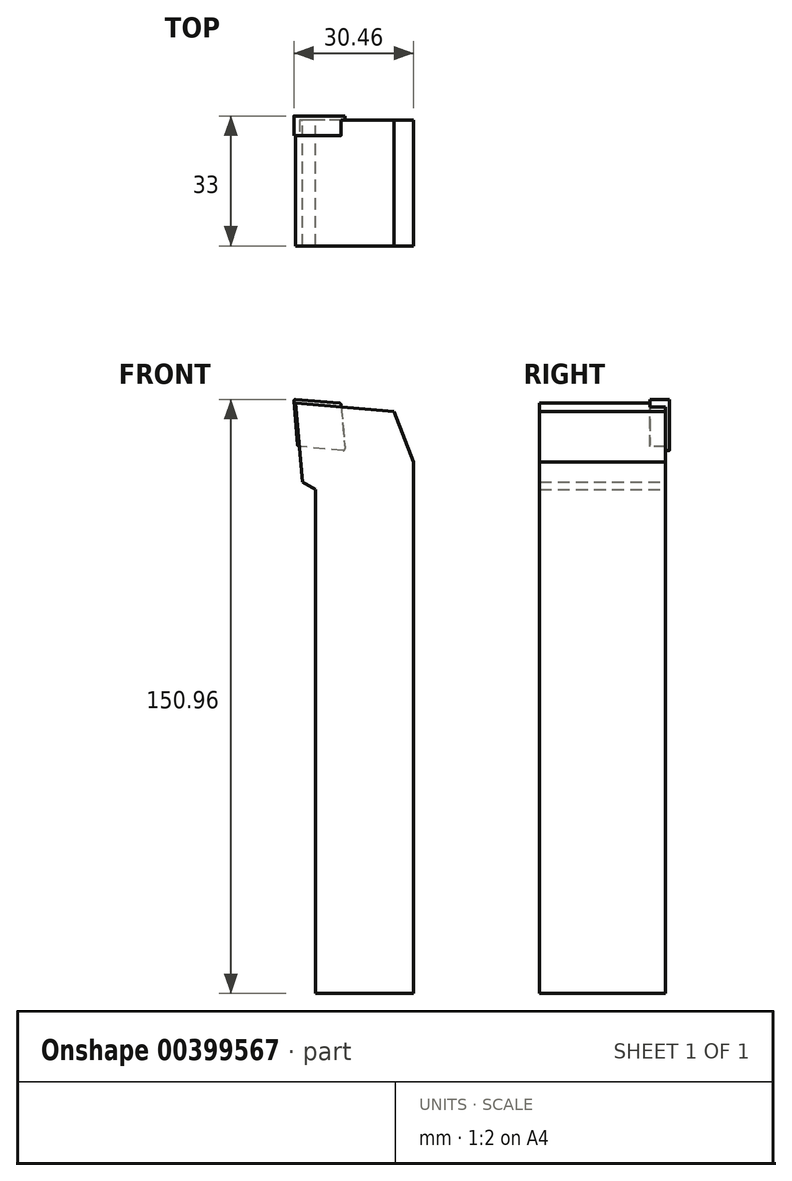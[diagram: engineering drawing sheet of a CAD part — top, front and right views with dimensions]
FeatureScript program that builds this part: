
annotation { "Feature Type Name" : "Feature", "Feature Type Description" : "" }
export const myFeature = defineFeature(function(context is Context, id is Id, definition is map)
    precondition{}
    {
        {
            var Q0;
            Q0=qCreatedBy(makeId("Front.planeOp"),FACE);
            var sketch = newSketch(context, id + "F0", { "sketchPlane" : qUnion([Q0])});
            skLineSegment(sketch, "E0", {"start": v(0, 0) * mm, "end": v(0, 128) * mm});
            skLineSegment(sketch, "E1", {"start": v(0, 128) * mm, "end": v(-3.25, 130) * mm});
            skLineSegment(sketch, "E2", {"start": v(25, 135) * mm, "end": v(25, 0) * mm});
            skLineSegment(sketch, "E3", {"start": v(25, 0) * mm, "end": v(0, 0) * mm});
            skLineSegment(sketch, "E4", {"start": v(20, 147.81) * mm, "end": v(25, 135) * mm});
            skLineSegment(sketch, "E5", {"start": v(-5, 150) * mm, "end": v(-3.25, 130) * mm});
            skLineSegment(sketch, "E6", {"start": v(-5, 150) * mm, "end": v(20, 147.81) * mm});
            skSolve(sketch);
        }
        {
            var Q0;
            Q0=makeQuery(id+"F0.imprint","IMPRINT",FACE,{"disambiguationData":[TD([[makeQuery(id+"F0.imprint","IMPRINT",EDGE,{"derivedFrom":sQuery(id+"F0.wireOp",EDGE,"E0")}),-1.0]])]});
            extrude(context, id + "F1", {"entities" : qUnion([Q0]), "depth" : 32 * mm});
        }
        {
            var Q0;
            Q0=makeQuery(id+"F1.opExtrude","CAP_FACE",FACE,{"disambiguationData":[OSD([sQuery(id+"F0.wireOp",EDGE,"E0"),sQuery(id+"F0.wireOp",EDGE,"E1"),sQuery(id+"F0.wireOp",EDGE,"E2"),sQuery(id+"F0.wireOp",EDGE,"E3"),sQuery(id+"F0.wireOp",EDGE,"EDo5xP3I-3DC5-2Pxk-wrLf-A15lKSKhXm15"),sQuery(id+"F0.wireOp",EDGE,"E4"),sQuery(id+"F0.wireOp",EDGE,"E5")])],"isStart":true});
            var sketch = newSketch(context, id + "F2", { "sketchPlane" : qUnion([Q0])});
            skLineSegment(sketch, "E7", {"start": v(5.5, 151) * mm, "end": v(4.45, 139) * mm});
            skLineSegment(sketch, "E8", {"start": v(5.5, 151) * mm, "end": v(-6.5, 149.95) * mm});
            skLineSegment(sketch, "E9", {"start": v(-6.5, 149.95) * mm, "end": v(-7.55, 137.95) * mm});
            skLineSegment(sketch, "E10", {"start": v(-7.55, 137.95) * mm, "end": v(4.45, 139) * mm});
            skSolve(sketch);
        }
        {
            var Q0;
            {var subQ0=sQuery(id+"F2.wireOp",EDGE,"E10");var subQ1=sQuery(id+"F2.wireOp",EDGE,"E9");var subQ2=makeQuery(id+"F2.imprint","INTERSECT",VERTEX,{"derivedFrom":[subQ1,subQ0]});Q0=makeQuery(id+"F2.imprint","IMPRINT",FACE,{"disambiguationData":[TD([[makeQuery(id+"F2.imprint","IMPRINT",EDGE,{"disambiguationData":[TD([[subQ2,1.0]])],"derivedFrom":subQ1}),1.0]])]});}
            var Q1;
            {var subQ8=sQuery(id+"F2.wireOp",EDGE,"E7");Q1=makeQuery(id+"F2.imprint","IMPRINT",FACE,{"disambiguationData":[TD([[makeQuery(id+"F2.imprint","IMPRINT",EDGE,{"derivedFrom":subQ8}),-1.0]])]});}
            extrude(context, id + "F3", {"entities" : qUnion([Q0, Q1]), "operationType" : NewBodyOperationType.ADD, "depth" : 1 * mm, "hasSecondDirection" : true, "secondDirectionOppositeDirection" : true, "secondDirectionDepth" : 4 * mm});
        }
        {
            var Q0;
            Q0=makeQuery(id+"F3.opExtrude","SWEPT_EDGE",EDGE,{"disambiguationData":[OSD([sQuery(id+"F2.wireOp",EDGE,"E7"),sQuery(id+"F2.wireOp",EDGE,"E8")])]});
            var Q1;
            Q1=makeQuery(id+"F3.opExtrude","SWEPT_EDGE",EDGE,{"disambiguationData":[OSD([sQuery(id+"F2.wireOp",EDGE,"E8"),sQuery(id+"F2.wireOp",EDGE,"E9")])]});
            var Q2;
            Q2=makeQuery(id+"F3.opExtrude","SWEPT_EDGE",EDGE,{"disambiguationData":[OSD([sQuery(id+"F2.wireOp",EDGE,"E7"),sQuery(id+"F2.wireOp",EDGE,"E10")])]});
            var Q3;
            Q3=makeQuery(id+"F3.opExtrude","SWEPT_EDGE",EDGE,{"disambiguationData":[OSD([sQuery(id+"F2.wireOp",EDGE,"E9"),sQuery(id+"F2.wireOp",EDGE,"E10")])]});
            fillet(context, id + "F4", {"entities" : qUnion([Q0, Q1, Q2, Q3]), "radius" : 0.4 * mm, "tangentPropagation" : true, "allowEdgeOverflow" : false});
        }
    });
